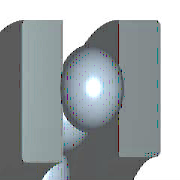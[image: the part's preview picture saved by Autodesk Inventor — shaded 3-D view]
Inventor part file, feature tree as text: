
AUTODESK INVENTOR PART (.ipt)
format: ipt  version: 2025 (Build 290162010, 162A)  size: 332,800 bytes
history: native  units: mm (DEFAULTED — no unit token found)
features: sketch x5, plane x4, other x3, hole x2, pattern_circular x1, fillet x1
ambient origin geometry x7: Origin, XZ Plane, XY Plane, X Axis, Y Axis, Z Axis, Center Point
bodies: Solid1 (feature_tree)
feature tree (16):
  plane  "WorkPlane1"
  sketch  "Sketch1"  dims[d0=-19.0mm d1=24.0mm]
  other  "WorkPoint1"
  plane  "Work Plane2"
  plane  "WorkPlane2"
  sketch  "Sketch3"  dims[d2=110.0mm d3=9.5mm]
  other  "WorkPoint2"
  other  "WorkAxis1"
  hole  "Hole1"  [1 undecoded]
  hole  "Hole2"  [1 undecoded]
  pattern_circular  "PolarArray1"  [2 undecoded]
  fillet  "Fillet1"  Radius=110.0mm
  plane  "WorkPlane3"
  sketch  "Sketch5"  dims[d4=0.0mm]
  sketch  "Sketch6"  dims[d5=0.0mm]
  sketch  "Sketch7"  dims[d6=0.0mm d7=24.0mm d8=110.0mm d9=9.5mm d10=0.0mm d11=0.0mm d12=85.0mm d13=6.0mm d14=4.0mm d15=2.0mm d16=60.0deg d17=9.5mm d18=20.594885mm d19=87.0mm d20=6.0mm d21=4.0mm d22=2.0mm d23=60.0deg d24=9.5mm d25=20.594885mm d26=2.52mm d27=4.5mm d28=360.0deg d29=2.52mm d30=4.5mm d31=360.0deg d32=160.0mm d34=360.0deg d35=1.0mm d36=19.0mm d37=6.333333mm d38=97.5mm d39=6.333333mm d40=97.5mm d43=0.0mm d44=0.0mm d45=0.0mm d46=0.0mm d47=0.0mm]
note: 4 required parameter values undecoded (feature->parameter linkage not recoverable at this tier; creation-order binding heuristic only, values carry confidence <= 0.55)
